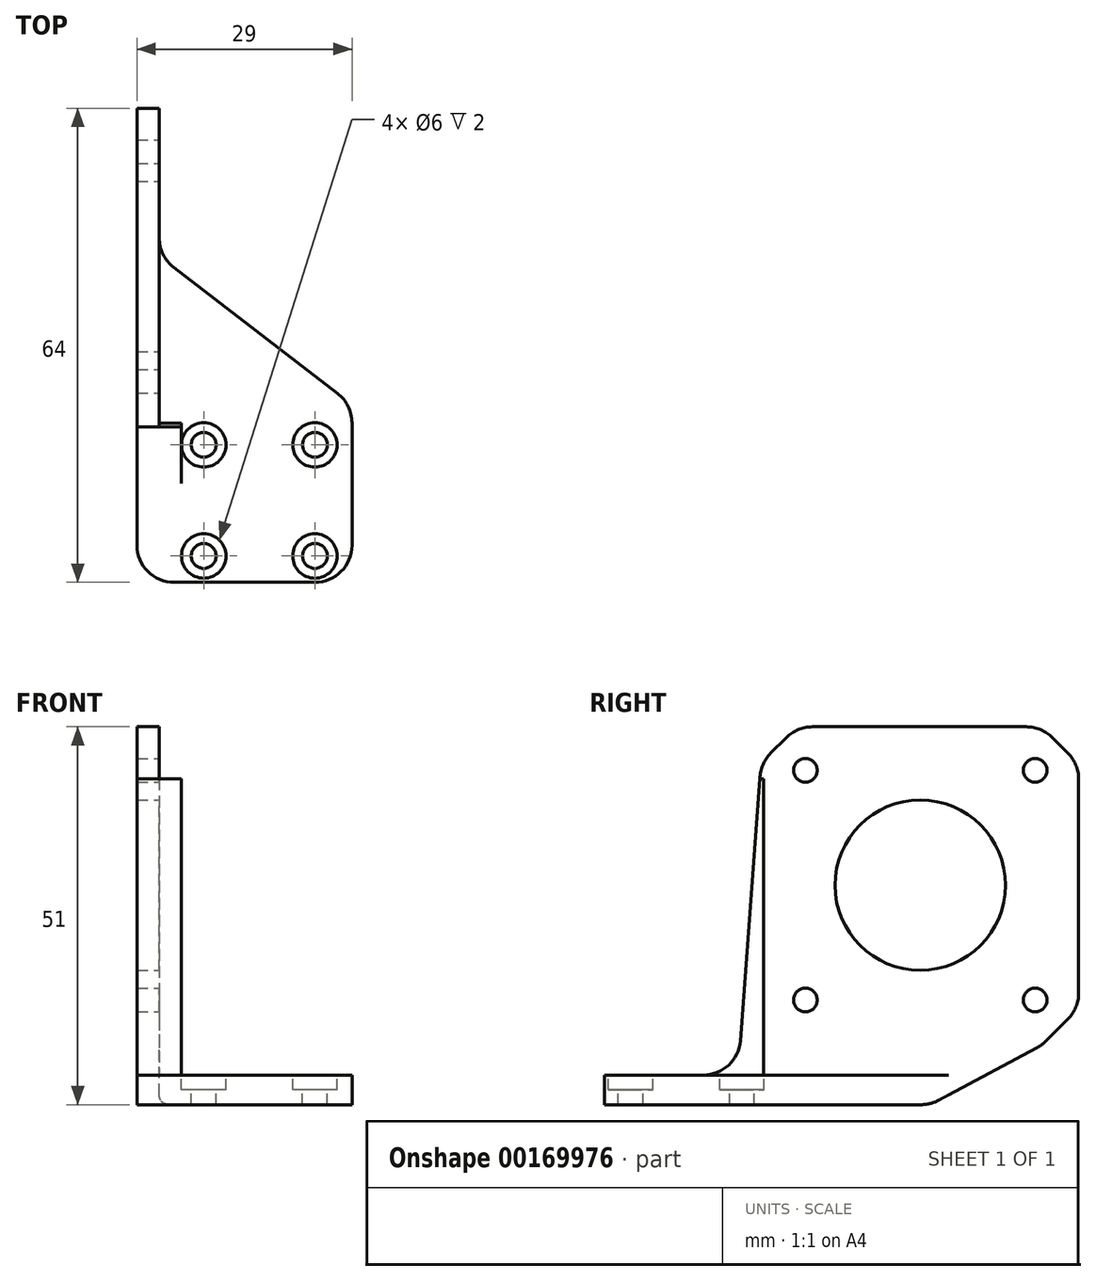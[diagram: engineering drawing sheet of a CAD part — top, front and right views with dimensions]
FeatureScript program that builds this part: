
annotation { "Feature Type Name" : "Feature", "Feature Type Description" : "" }
export const myFeature = defineFeature(function(context is Context, id is Id, definition is map)
    precondition{}
    {
        {
            var Q0;
            Q0=qCreatedBy(makeId("Top.planeOp"),FACE);
            var sketch = newSketch(context, id + "F0", { "sketchPlane" : qUnion([Q0])});
            skLineSegment(sketch, "E0.bottom", {"start": v(0, 0) * mm, "end": v(29, 0) * mm});
            skLineSegment(sketch, "E0.top", {"start": v(0, 44) * mm, "end": v(29, 44) * mm});
            skLineSegment(sketch, "E0.left", {"start": v(0, 0) * mm, "end": v(0, 44) * mm});
            skLineSegment(sketch, "E0.right", {"start": v(29, 0) * mm, "end": v(29, 44) * mm});
            skSolve(sketch);
        }
        {
            var Q0;
            Q0=qSketchRegion(id+"F0",true);
            extrude(context, id + "F1", {"entities" : qUnion([Q0]), "depth" : 4 * mm});
        }
        {
            var Q0;
            Q0=makeQuery(id+"F1.opExtrude","CAP_FACE",FACE,{"disambiguationData":[OSD([sQuery(id+"F0.wireOp",EDGE,"E0.bottom"),sQuery(id+"F0.wireOp",EDGE,"E0.top"),sQuery(id+"F0.wireOp",EDGE,"E0.left"),sQuery(id+"F0.wireOp",EDGE,"E0.right")])],"isStart":false});
            var sketch = newSketch(context, id + "F2", { "sketchPlane" : qUnion([Q0])});
            skCircle(sketch, "E1", {"center": v(9, 18.56) * mm, "radius": 1.68 * mm});
            skCircle(sketch, "E2", {"center": v(24, 18.56) * mm, "radius": 1.68 * mm});
            skCircle(sketch, "E3", {"center": v(9, 3.56) * mm, "radius": 1.68 * mm});
            skCircle(sketch, "E4", {"center": v(24, 3.56) * mm, "radius": 1.68 * mm});
            skLineSegment(sketch, "E5", {"start": v(24, 3.56) * mm, "end": v(29, 3.56) * mm});
            skCircle(sketch, "E6", {"center": v(9, 18.56) * mm, "radius": 3 * mm});
            skCircle(sketch, "E7", {"center": v(24, 18.56) * mm, "radius": 3 * mm});
            skCircle(sketch, "E8", {"center": v(9, 3.56) * mm, "radius": 3 * mm});
            skCircle(sketch, "E9", {"center": v(24, 3.56) * mm, "radius": 3 * mm});
            skSolve(sketch);
        }
        {
            var Q0;
            Q0=makeQuery(id+"F2.imprint","IMPRINT",FACE,{"disambiguationData":[TD([[makeQuery(id+"F2.imprint","IMPRINT",EDGE,{"derivedFrom":sQuery(id+"F2.wireOp",EDGE,"E1")}),1.0]])]});
            var Q1;
            Q1=makeQuery(id+"F2.imprint","IMPRINT",FACE,{"disambiguationData":[TD([[makeQuery(id+"F2.imprint","IMPRINT",EDGE,{"derivedFrom":sQuery(id+"F2.wireOp",EDGE,"E2")}),1.0]])]});
            var Q2;
            Q2=makeQuery(id+"F2.imprint","IMPRINT",FACE,{"disambiguationData":[TD([[makeQuery(id+"F2.imprint","IMPRINT",EDGE,{"derivedFrom":sQuery(id+"F2.wireOp",EDGE,"E4")}),1.0]])]});
            var Q3;
            Q3=makeQuery(id+"F2.imprint","IMPRINT",FACE,{"disambiguationData":[TD([[makeQuery(id+"F2.imprint","IMPRINT",EDGE,{"derivedFrom":sQuery(id+"F2.wireOp",EDGE,"E3")}),1.0]])]});
            extrude(context, id + "F3", {"entities" : qUnion([Q0, Q1, Q2, Q3]), "operationType" : NewBodyOperationType.REMOVE, "oppositeDirection" : true, "depth" : 25 * mm});
        }
        {
            var Q0;
            Q0=makeQuery(id+"F2.imprint","IMPRINT",FACE,{"disambiguationData":[TD([[makeQuery(id+"F2.imprint","IMPRINT",EDGE,{"derivedFrom":sQuery(id+"F2.wireOp",EDGE,"E1")}),-1.0]])]});
            var Q1;
            Q1=makeQuery(id+"F2.imprint","IMPRINT",FACE,{"disambiguationData":[TD([[makeQuery(id+"F2.imprint","IMPRINT",EDGE,{"derivedFrom":sQuery(id+"F2.wireOp",EDGE,"E2")}),-1.0]])]});
            var Q2;
            Q2=makeQuery(id+"F2.imprint","IMPRINT",FACE,{"disambiguationData":[TD([[makeQuery(id+"F2.imprint","IMPRINT",EDGE,{"derivedFrom":sQuery(id+"F2.wireOp",EDGE,"E4")}),-1.0]])]});
            var Q3;
            Q3=makeQuery(id+"F2.imprint","IMPRINT",FACE,{"disambiguationData":[TD([[makeQuery(id+"F2.imprint","IMPRINT",EDGE,{"derivedFrom":sQuery(id+"F2.wireOp",EDGE,"E3")}),-1.0]])]});
            extrude(context, id + "F4", {"entities" : qUnion([Q0, Q1, Q2, Q3]), "operationType" : NewBodyOperationType.REMOVE, "oppositeDirection" : true, "depth" : 2 * mm});
        }
        {
            var Q0;
            Q0=makeQuery(id+"F1.opExtrude","CAP_FACE",FACE,{"disambiguationData":[OSD([sQuery(id+"F0.wireOp",EDGE,"E0.bottom"),sQuery(id+"F0.wireOp",EDGE,"E0.top"),sQuery(id+"F0.wireOp",EDGE,"E0.left"),sQuery(id+"F0.wireOp",EDGE,"E0.right")])],"isStart":false});
            var sketch = newSketch(context, id + "F5", { "sketchPlane" : qUnion([Q0])});
            skLineSegment(sketch, "E10.bottom", {"start": v(0, 21) * mm, "end": v(3, 21) * mm});
            skLineSegment(sketch, "E10.top", {"start": v(0, 44) * mm, "end": v(3, 44) * mm});
            skLineSegment(sketch, "E10.left", {"start": v(0, 21) * mm, "end": v(0, 44) * mm});
            skLineSegment(sketch, "E10.right", {"start": v(3, 21) * mm, "end": v(3, 44) * mm});
            skSolve(sketch);
        }
        {
            var Q0;
            Q0=makeQuery(id+"F5.imprint","IMPRINT",FACE,{"disambiguationData":[TD([[makeQuery(id+"F5.imprint","IMPRINT",EDGE,{"derivedFrom":sQuery(id+"F5.wireOp",EDGE,"E10.bottom")}),1.0]])]});
            extrude(context, id + "F6", {"entities" : qUnion([Q0]), "operationType" : NewBodyOperationType.ADD, "depth" : 47 * mm});
        }
        {
            var Q0;
            Q0=makeQuery(id+"F6.boolean.opBoolean","MERGE",FACE,{"derivedFrom":[makeQuery(id+"F1.opExtrude","SWEPT_FACE",FACE,{"disambiguationData":[OSD([sQuery(id+"F0.wireOp",EDGE,"E0.top")])]}),makeQuery(id+"F6.opExtrude","SWEPT_FACE",FACE,{"disambiguationData":[OSD([sQuery(id+"F5.wireOp",EDGE,"E10.top")])]})]});
            var sketch = newSketch(context, id + "F7", { "sketchPlane" : qUnion([Q0])});
            skLineSegment(sketch, "E11.bottom", {"start": v(0, 51) * mm, "end": v(-3, 51) * mm});
            skLineSegment(sketch, "E11.top", {"start": v(0, 8) * mm, "end": v(-3, 8) * mm});
            skLineSegment(sketch, "E11.left", {"start": v(0, 51) * mm, "end": v(0, 8) * mm});
            skLineSegment(sketch, "E11.right", {"start": v(-3, 51) * mm, "end": v(-3, 8) * mm});
            skSolve(sketch);
        }
        {
            var Q0;
            Q0=makeQuery(id+"F7.imprint","IMPRINT",FACE,{"disambiguationData":[TD([[makeQuery(id+"F7.imprint","IMPRINT",EDGE,{"derivedFrom":sQuery(id+"F7.wireOp",EDGE,"E11.bottom")}),1.0]])]});
            extrude(context, id + "F8", {"entities" : qUnion([Q0]), "operationType" : NewBodyOperationType.ADD, "depth" : 20 * mm});
        }
        {
            var Q0;
            Q0=makeQuery(id+"F8.opExtrude","CAP_EDGE",EDGE,{"disambiguationData":[OSD([sQuery(id+"F7.wireOp",EDGE,"E11.top")])],"isStart":false});
            var Q1;
            Q1=makeQuery(id+"F8.opExtrude","CAP_EDGE",EDGE,{"disambiguationData":[OSD([sQuery(id+"F7.wireOp",EDGE,"E11.bottom")])],"isStart":false});
            var Q2;
            Q2=makeQuery(id+"F6.opExtrude","CAP_EDGE",EDGE,{"disambiguationData":[OSD([sQuery(id+"F5.wireOp",EDGE,"E10.bottom")])],"isStart":false});
            chamfer(context, id + "F9", {"entities" : qUnion([Q0, Q1, Q2]), "width" : 5 * mm, "tangentPropagation" : true});
        }
        {
            var Q0;
            Q0=makeQuery(id+"F8.boolean.opBoolean","MERGE",FACE,{"derivedFrom":[makeQuery(id+"F6.boolean.opBoolean","MERGE",FACE,{"derivedFrom":[makeQuery(id+"F1.opExtrude","SWEPT_FACE",FACE,{"disambiguationData":[OSD([sQuery(id+"F0.wireOp",EDGE,"E0.left")])]}),makeQuery(id+"F6.opExtrude","SWEPT_FACE",FACE,{"disambiguationData":[OSD([sQuery(id+"F5.wireOp",EDGE,"E10.left")])]})]}),makeQuery(id+"F8.opExtrude","SWEPT_FACE",FACE,{"disambiguationData":[OSD([sQuery(id+"F7.wireOp",EDGE,"E11.left")])]})]});
            var sketch = newSketch(context, id + "F10", { "sketchPlane" : qUnion([Q0])});
            skLineSegment(sketch, "E12", {"start": v(-59, 8) * mm, "end": v(-44, 0) * mm});
            skSolve(sketch);
        }
        {
            var Q0;
            Q0=makeQuery(id+"F10.imprint","IMPRINT",FACE,{"disambiguationData":[TD([[makeQuery(id+"F10.imprint","IMPRINT",EDGE,{"derivedFrom":sQuery(id+"F10.wireOp",EDGE,"E12")}),1.0]])]});
            var Q1;
            Q1=makeQuery(id+"F8.boolean.opBoolean","MERGE",FACE,{"derivedFrom":[makeQuery(id+"F6.opExtrude","SWEPT_FACE",FACE,{"disambiguationData":[OSD([sQuery(id+"F5.wireOp",EDGE,"E10.right")])]}),makeQuery(id+"F8.opExtrude","SWEPT_FACE",FACE,{"disambiguationData":[OSD([sQuery(id+"F7.wireOp",EDGE,"E11.right")])]})]});
            extrude(context, id + "F11", {"entities" : qUnion([Q0]), "operationType" : NewBodyOperationType.ADD, "endBound" : BoundingType.UP_TO_SURFACE, "oppositeDirection" : true, "endBoundEntityFace" : qUnion([Q1]), "depth" : 25 * mm});
        }
        {
            var Q0;
            {var subQ0=sQuery(id+"F7.wireOp",EDGE,"E11.right");var subQ1=sQuery(id+"F5.wireOp",EDGE,"E10.right");Q0=makeQuery(id+"F11.boolean.opBoolean","MERGE",FACE,{"derivedFrom":[makeQuery(id+"F8.boolean.opBoolean","MERGE",FACE,{"derivedFrom":[makeQuery(id+"F6.opExtrude","SWEPT_FACE",FACE,{"disambiguationData":[OSD([subQ1])]}),makeQuery(id+"F8.opExtrude","SWEPT_FACE",FACE,{"disambiguationData":[OSD([subQ0])]})]}),makeQuery(id+"F11.opExtrude","CAP_FACE",FACE,{"disambiguationData":[OSD([subQ1,subQ0])],"isStart":false})]});}
            var sketch = newSketch(context, id + "F12", { "sketchPlane" : qUnion([Q0])});
            skCircle(sketch, "E13", {"center": v(42.62, 29.63) * mm, "radius": 11.5 * mm});
            skPoint(sketch, "E13.centerSnap0", {"position": v(64.25, 29.63) * mm});
            skLineSegment(sketch, "E14.bottom", {"start": v(58.12, 14.12) * mm, "end": v(27.12, 14.12) * mm, "construction": true});
            skLineSegment(sketch, "E14.top", {"start": v(58.12, 45.12) * mm, "end": v(27.12, 45.12) * mm, "construction": true});
            skLineSegment(sketch, "E14.left", {"start": v(58.12, 14.12) * mm, "end": v(58.12, 45.12) * mm, "construction": true});
            skLineSegment(sketch, "E14.right", {"start": v(27.12, 14.12) * mm, "end": v(27.12, 45.12) * mm, "construction": true});
            skCircle(sketch, "E15", {"center": v(58.12, 45.12) * mm, "radius": 1.6 * mm});
            skCircle(sketch, "E16", {"center": v(58.12, 14.12) * mm, "radius": 1.6 * mm});
            skCircle(sketch, "E17", {"center": v(27.12, 14.12) * mm, "radius": 1.6 * mm});
            skCircle(sketch, "E18", {"center": v(27.12, 45.12) * mm, "radius": 1.6 * mm});
            skSolve(sketch);
        }
        {
            var Q0;
            Q0=makeQuery(id+"F12.imprint","IMPRINT",FACE,{"disambiguationData":[TD([[makeQuery(id+"F12.imprint","IMPRINT",EDGE,{"derivedFrom":sQuery(id+"F12.wireOp",EDGE,"E13")}),1.0]])]});
            var Q1;
            Q1=makeQuery(id+"F12.imprint","IMPRINT",FACE,{"disambiguationData":[TD([[makeQuery(id+"F12.imprint","IMPRINT",EDGE,{"derivedFrom":sQuery(id+"F12.wireOp",EDGE,"E15")}),1.0]])]});
            var Q2;
            Q2=makeQuery(id+"F12.imprint","IMPRINT",FACE,{"disambiguationData":[TD([[makeQuery(id+"F12.imprint","IMPRINT",EDGE,{"derivedFrom":sQuery(id+"F12.wireOp",EDGE,"E16")}),1.0]])]});
            var Q3;
            Q3=makeQuery(id+"F12.imprint","IMPRINT",FACE,{"disambiguationData":[TD([[makeQuery(id+"F12.imprint","IMPRINT",EDGE,{"derivedFrom":sQuery(id+"F12.wireOp",EDGE,"E18")}),1.0]])]});
            var Q4;
            Q4=makeQuery(id+"F12.imprint","IMPRINT",FACE,{"disambiguationData":[TD([[makeQuery(id+"F12.imprint","IMPRINT",EDGE,{"derivedFrom":sQuery(id+"F12.wireOp",EDGE,"E17")}),1.0]])]});
            extrude(context, id + "F13", {"entities" : qUnion([Q0, Q1, Q2, Q3, Q4]), "operationType" : NewBodyOperationType.REMOVE, "endBound" : BoundingType.UP_TO_NEXT, "oppositeDirection" : true, "depth" : 25 * mm});
        }
        {
            var Q0;
            Q0=makeQuery(id+"F1.opExtrude","SWEPT_EDGE",EDGE,{"disambiguationData":[OSD([sQuery(id+"F0.wireOp",EDGE,"E0.top"),sQuery(id+"F0.wireOp",EDGE,"E0.right")])]});
            chamfer(context, id + "F14", {"entities" : qUnion([Q0]), "chamferType" : ChamferType.TWO_OFFSETS, "width1" : 26 * mm, "oppositeDirection" : false, "width2" : 20 * mm, "tangentPropagation" : true});
        }
        {
            var Q0;
            Q0=makeQuery(id+"F1.opExtrude","CAP_FACE",FACE,{"disambiguationData":[OSD([sQuery(id+"F0.wireOp",EDGE,"E0.bottom"),sQuery(id+"F0.wireOp",EDGE,"E0.top"),sQuery(id+"F0.wireOp",EDGE,"E0.left"),sQuery(id+"F0.wireOp",EDGE,"E0.right")])],"isStart":false});
            var sketch = newSketch(context, id + "F15", { "sketchPlane" : qUnion([Q0])});
            skLineSegment(sketch, "E19.bottom", {"start": v(3, 21.5) * mm, "end": v(6, 21.5) * mm});
            skLineSegment(sketch, "E19.top", {"start": v(0, 18) * mm, "end": v(6.05, 18) * mm});
            skLineSegment(sketch, "E19.left", {"start": v(0, 21) * mm, "end": v(0, 18) * mm});
            skLineSegment(sketch, "E19.right", {"start": v(6, 21.5) * mm, "end": v(6, 18) * mm});
            skLineSegment(sketch, "E20", {"start": v(3, 21.5) * mm, "end": v(3, 21) * mm});
            skLineSegment(sketch, "E21", {"start": v(3, 21) * mm, "end": v(0, 21) * mm});
            skSolve(sketch);
        }
        {
            var Q0;
            {var subQ0=sQuery(id+"F15.wireOp",EDGE,"E19.left");Q0=makeQuery(id+"F15.imprint","IMPRINT",FACE,{"disambiguationData":[TD([[makeQuery(id+"F15.imprint","IMPRINT",EDGE,{"derivedFrom":subQ0}),-1.0]])]});}
            extrude(context, id + "F16", {"entities" : qUnion([Q0]), "operationType" : NewBodyOperationType.ADD, "depth" : 40 * mm});
        }
        {
            var Q0;
            Q0=makeQuery(id+"F16.opExtrude","CAP_EDGE",EDGE,{"disambiguationData":[OSD([sQuery(id+"F15.wireOp",EDGE,"E19.top")])],"isStart":false});
            chamfer(context, id + "F17", {"entities" : qUnion([Q0]), "chamferType" : ChamferType.TWO_OFFSETS, "width1" : 3 * mm, "oppositeDirection" : false, "width2" : 40 * mm, "tangentPropagation" : true});
        }
        {
            var Q0;
            Q0=makeQuery(id+"F1.opExtrude","SWEPT_EDGE",EDGE,{"disambiguationData":[OSD([sQuery(id+"F0.wireOp",EDGE,"E0.bottom"),sQuery(id+"F0.wireOp",EDGE,"E0.left")])]});
            var Q1;
            Q1=makeQuery(id+"F1.opExtrude","SWEPT_EDGE",EDGE,{"disambiguationData":[OSD([sQuery(id+"F0.wireOp",EDGE,"E0.bottom"),sQuery(id+"F0.wireOp",EDGE,"E0.right")])]});
            var Q2;
            {var subQ0=sQuery(id+"F0.wireOp",EDGE,"E0.right");Q2=makeQuery(id+"F14.opChamfer","BLEND_EDGE",EDGE,{"blendedFrom":[makeQuery(id+"F1.opExtrude","SWEPT_EDGE",EDGE,{"disambiguationData":[OSD([sQuery(id+"F0.wireOp",EDGE,"E0.top"),subQ0])]}),makeQuery(id+"F1.opExtrude","SWEPT_FACE",FACE,{"disambiguationData":[OSD([subQ0])]})],"blendedInto":[makeQuery(id+"F1.opExtrude","SWEPT_FACE",FACE,{"disambiguationData":[OSD([subQ0])]})]});}
            var Q3;
            {var subQ0=sQuery(id+"F5.wireOp",EDGE,"E10.bottom");Q3=makeQuery(id+"FskCs65OhL5Ulzs_1.boolean.opBoolean","MERGE",EDGE,{"derivedFrom":[makeQuery(id+"F9.opChamfer","BLEND_EDGE",EDGE,{"blendedFrom":[makeQuery(id+"F6.opExtrude","CAP_EDGE",EDGE,{"disambiguationData":[OSD([subQ0])],"isStart":false}),makeQuery(id+"F6.opExtrude","SWEPT_FACE",FACE,{"disambiguationData":[OSD([subQ0])]})],"blendedInto":[makeQuery(id+"F6.opExtrude","SWEPT_FACE",FACE,{"disambiguationData":[OSD([subQ0])]})]}),makeQuery(id+"FskCs65OhL5Ulzs_1.opExtrude","SWEPT_EDGE",EDGE,{"disambiguationData":[OSD([sQuery(id+"F0.wireOp",EDGE,"E0.left"),subQ0,sQuery(id+"F5.wireOp",EDGE,"E10.left"),sQuery(id+"F7.wireOp",EDGE,"E11.left"),sQuery(id+"FcdBgYlTXM9ahIo_1.wireOp",EDGE,"9GjrHczZ-MlOJ-sooe-1AeO-juJtFMyKNNtB")])]})]});}
            var Q4;
            {var subQ0=sQuery(id+"F5.wireOp",EDGE,"E10.bottom");Q4=makeQuery(id+"F9.opChamfer","BLEND_EDGE",EDGE,{"blendedFrom":[makeQuery(id+"F6.opExtrude","CAP_EDGE",EDGE,{"disambiguationData":[OSD([subQ0])],"isStart":false}),makeQuery(id+"F8.boolean.opBoolean","MERGE",FACE,{"derivedFrom":[makeQuery(id+"F6.opExtrude","CAP_FACE",FACE,{"disambiguationData":[OSD([subQ0,sQuery(id+"F5.wireOp",EDGE,"E10.top"),sQuery(id+"F5.wireOp",EDGE,"E10.left"),sQuery(id+"F5.wireOp",EDGE,"E10.right")])],"isStart":false}),makeQuery(id+"F8.opExtrude","SWEPT_FACE",FACE,{"disambiguationData":[OSD([sQuery(id+"F7.wireOp",EDGE,"E11.bottom")])]})]})],"blendedInto":[makeQuery(id+"F8.boolean.opBoolean","MERGE",FACE,{"derivedFrom":[makeQuery(id+"F6.opExtrude","CAP_FACE",FACE,{"disambiguationData":[OSD([subQ0,sQuery(id+"F5.wireOp",EDGE,"E10.top"),sQuery(id+"F5.wireOp",EDGE,"E10.left"),sQuery(id+"F5.wireOp",EDGE,"E10.right")])],"isStart":false}),makeQuery(id+"F8.opExtrude","SWEPT_FACE",FACE,{"disambiguationData":[OSD([sQuery(id+"F7.wireOp",EDGE,"E11.bottom")])]})]})]});}
            var Q5;
            {var subQ0=sQuery(id+"F7.wireOp",EDGE,"E11.bottom");Q5=makeQuery(id+"F9.opChamfer","BLEND_EDGE",EDGE,{"blendedFrom":[makeQuery(id+"F8.opExtrude","CAP_EDGE",EDGE,{"disambiguationData":[OSD([subQ0])],"isStart":false}),makeQuery(id+"F8.boolean.opBoolean","MERGE",FACE,{"derivedFrom":[makeQuery(id+"F6.opExtrude","CAP_FACE",FACE,{"disambiguationData":[OSD([sQuery(id+"F5.wireOp",EDGE,"E10.bottom"),sQuery(id+"F5.wireOp",EDGE,"E10.top"),sQuery(id+"F5.wireOp",EDGE,"E10.left"),sQuery(id+"F5.wireOp",EDGE,"E10.right")])],"isStart":false}),makeQuery(id+"F8.opExtrude","SWEPT_FACE",FACE,{"disambiguationData":[OSD([subQ0])]})]})],"blendedInto":[makeQuery(id+"F8.boolean.opBoolean","MERGE",FACE,{"derivedFrom":[makeQuery(id+"F6.opExtrude","CAP_FACE",FACE,{"disambiguationData":[OSD([sQuery(id+"F5.wireOp",EDGE,"E10.bottom"),sQuery(id+"F5.wireOp",EDGE,"E10.top"),sQuery(id+"F5.wireOp",EDGE,"E10.left"),sQuery(id+"F5.wireOp",EDGE,"E10.right")])],"isStart":false}),makeQuery(id+"F8.opExtrude","SWEPT_FACE",FACE,{"disambiguationData":[OSD([subQ0])]})]})]});}
            var Q6;
            {var subQ0=sQuery(id+"F7.wireOp",EDGE,"E11.bottom");Q6=makeQuery(id+"F9.opChamfer","BLEND_EDGE",EDGE,{"blendedFrom":[makeQuery(id+"F8.opExtrude","CAP_EDGE",EDGE,{"disambiguationData":[OSD([subQ0])],"isStart":false}),makeQuery(id+"F8.opExtrude","CAP_FACE",FACE,{"disambiguationData":[OSD([subQ0,sQuery(id+"F7.wireOp",EDGE,"E11.top"),sQuery(id+"F7.wireOp",EDGE,"E11.left"),sQuery(id+"F7.wireOp",EDGE,"E11.right")])],"isStart":false})],"blendedInto":[makeQuery(id+"F8.opExtrude","CAP_FACE",FACE,{"disambiguationData":[OSD([subQ0,sQuery(id+"F7.wireOp",EDGE,"E11.top"),sQuery(id+"F7.wireOp",EDGE,"E11.left"),sQuery(id+"F7.wireOp",EDGE,"E11.right")])],"isStart":false})]});}
            var Q7;
            {var subQ0=sQuery(id+"F7.wireOp",EDGE,"E11.top");Q7=makeQuery(id+"F9.opChamfer","BLEND_EDGE",EDGE,{"blendedFrom":[makeQuery(id+"F8.opExtrude","CAP_EDGE",EDGE,{"disambiguationData":[OSD([subQ0])],"isStart":false}),makeQuery(id+"F8.opExtrude","CAP_FACE",FACE,{"disambiguationData":[OSD([sQuery(id+"F7.wireOp",EDGE,"E11.bottom"),subQ0,sQuery(id+"F7.wireOp",EDGE,"E11.left"),sQuery(id+"F7.wireOp",EDGE,"E11.right")])],"isStart":false})],"blendedInto":[makeQuery(id+"F8.opExtrude","CAP_FACE",FACE,{"disambiguationData":[OSD([sQuery(id+"F7.wireOp",EDGE,"E11.bottom"),subQ0,sQuery(id+"F7.wireOp",EDGE,"E11.left"),sQuery(id+"F7.wireOp",EDGE,"E11.right")])],"isStart":false})]});}
            var Q8;
            {var subQ0=sQuery(id+"F7.wireOp",EDGE,"E11.top");Q8=makeQuery(id+"F11.boolean.opBoolean","MERGE",EDGE,{"derivedFrom":[makeQuery(id+"F9.opChamfer","BLEND_EDGE",EDGE,{"blendedFrom":[makeQuery(id+"F8.opExtrude","CAP_EDGE",EDGE,{"disambiguationData":[OSD([subQ0])],"isStart":false}),makeQuery(id+"F8.opExtrude","SWEPT_FACE",FACE,{"disambiguationData":[OSD([subQ0])]})],"blendedInto":[makeQuery(id+"F8.opExtrude","SWEPT_FACE",FACE,{"disambiguationData":[OSD([subQ0])]})]}),makeQuery(id+"F11.opExtrude","SWEPT_EDGE",EDGE,{"disambiguationData":[OSD([sQuery(id+"F0.wireOp",EDGE,"E0.top"),sQuery(id+"F0.wireOp",EDGE,"E0.left"),sQuery(id+"F5.wireOp",EDGE,"E10.top"),sQuery(id+"F5.wireOp",EDGE,"E10.left"),subQ0,sQuery(id+"F7.wireOp",EDGE,"E11.left"),sQuery(id+"F10.wireOp",EDGE,"E12")])]})]});}
            var Q9;
            {var subQ0=sQuery(id+"F7.wireOp",EDGE,"E11.right");var subQ1=sQuery(id+"F5.wireOp",EDGE,"E10.right");Q9=makeQuery(id+"F14.opChamfer","BLEND_EDGE",EDGE,{"blendedFrom":[makeQuery(id+"F1.opExtrude","SWEPT_EDGE",EDGE,{"disambiguationData":[OSD([sQuery(id+"F0.wireOp",EDGE,"E0.top"),sQuery(id+"F0.wireOp",EDGE,"E0.right")])]}),makeQuery(id+"FskCs65OhL5Ulzs_1.boolean.opBoolean","MERGE",FACE,{"derivedFrom":[makeQuery(id+"F11.boolean.opBoolean","MERGE",FACE,{"derivedFrom":[makeQuery(id+"F8.boolean.opBoolean","MERGE",FACE,{"derivedFrom":[makeQuery(id+"F6.opExtrude","SWEPT_FACE",FACE,{"disambiguationData":[OSD([subQ1])]}),makeQuery(id+"F8.opExtrude","SWEPT_FACE",FACE,{"disambiguationData":[OSD([subQ0])]})]}),makeQuery(id+"F11.opExtrude","CAP_FACE",FACE,{"disambiguationData":[OSD([subQ1,subQ0])],"isStart":false})]}),makeQuery(id+"FskCs65OhL5Ulzs_1.opExtrude","CAP_FACE",FACE,{"disambiguationData":[OSD([subQ1,subQ0])],"isStart":false})]})],"blendedInto":[makeQuery(id+"FskCs65OhL5Ulzs_1.boolean.opBoolean","MERGE",FACE,{"derivedFrom":[makeQuery(id+"F11.boolean.opBoolean","MERGE",FACE,{"derivedFrom":[makeQuery(id+"F8.boolean.opBoolean","MERGE",FACE,{"derivedFrom":[makeQuery(id+"F6.opExtrude","SWEPT_FACE",FACE,{"disambiguationData":[OSD([subQ1])]}),makeQuery(id+"F8.opExtrude","SWEPT_FACE",FACE,{"disambiguationData":[OSD([subQ0])]})]}),makeQuery(id+"F11.opExtrude","CAP_FACE",FACE,{"disambiguationData":[OSD([subQ1,subQ0])],"isStart":false})]}),makeQuery(id+"FskCs65OhL5Ulzs_1.opExtrude","CAP_FACE",FACE,{"disambiguationData":[OSD([subQ1,subQ0])],"isStart":false})]})]});}
            var Q10;
            {var subQ0=sQuery(id+"F0.wireOp",EDGE,"E0.top");Q10=makeQuery(id+"F11.boolean.opBoolean","MERGE",EDGE,{"derivedFrom":[makeQuery(id+"F1.opExtrude","CAP_EDGE",EDGE,{"disambiguationData":[OSD([subQ0])],"isStart":true}),makeQuery(id+"F11.opExtrude","SWEPT_EDGE",EDGE,{"disambiguationData":[OSD([subQ0,sQuery(id+"F0.wireOp",EDGE,"E0.left"),sQuery(id+"F5.wireOp",EDGE,"E10.top"),sQuery(id+"F5.wireOp",EDGE,"E10.left"),sQuery(id+"F10.wireOp",EDGE,"E12")])]})]});}
            var Q11;
            Q11=makeQuery(id+"F17.opChamfer","BLEND_EDGE",EDGE,{"blendedFrom":[makeQuery(id+"F16.opExtrude","CAP_EDGE",EDGE,{"disambiguationData":[OSD([sQuery(id+"F15.wireOp",EDGE,"E19.top")])],"isStart":false}),makeQuery(id+"F1.opExtrude","CAP_FACE",FACE,{"disambiguationData":[OSD([sQuery(id+"F0.wireOp",EDGE,"E0.bottom"),sQuery(id+"F0.wireOp",EDGE,"E0.top"),sQuery(id+"F0.wireOp",EDGE,"E0.left"),sQuery(id+"F0.wireOp",EDGE,"E0.right")])],"isStart":false})],"blendedInto":[makeQuery(id+"F1.opExtrude","CAP_FACE",FACE,{"disambiguationData":[OSD([sQuery(id+"F0.wireOp",EDGE,"E0.bottom"),sQuery(id+"F0.wireOp",EDGE,"E0.top"),sQuery(id+"F0.wireOp",EDGE,"E0.left"),sQuery(id+"F0.wireOp",EDGE,"E0.right")])],"isStart":false})]});
            fillet(context, id + "F18", {"entities" : qUnion([Q0, Q1, Q2, Q3, Q4, Q5, Q6, Q7, Q8, Q9, Q10, Q11]), "radius" : 5 * mm, "tangentPropagation" : true, "allowEdgeOverflow" : false});
        }
    });
